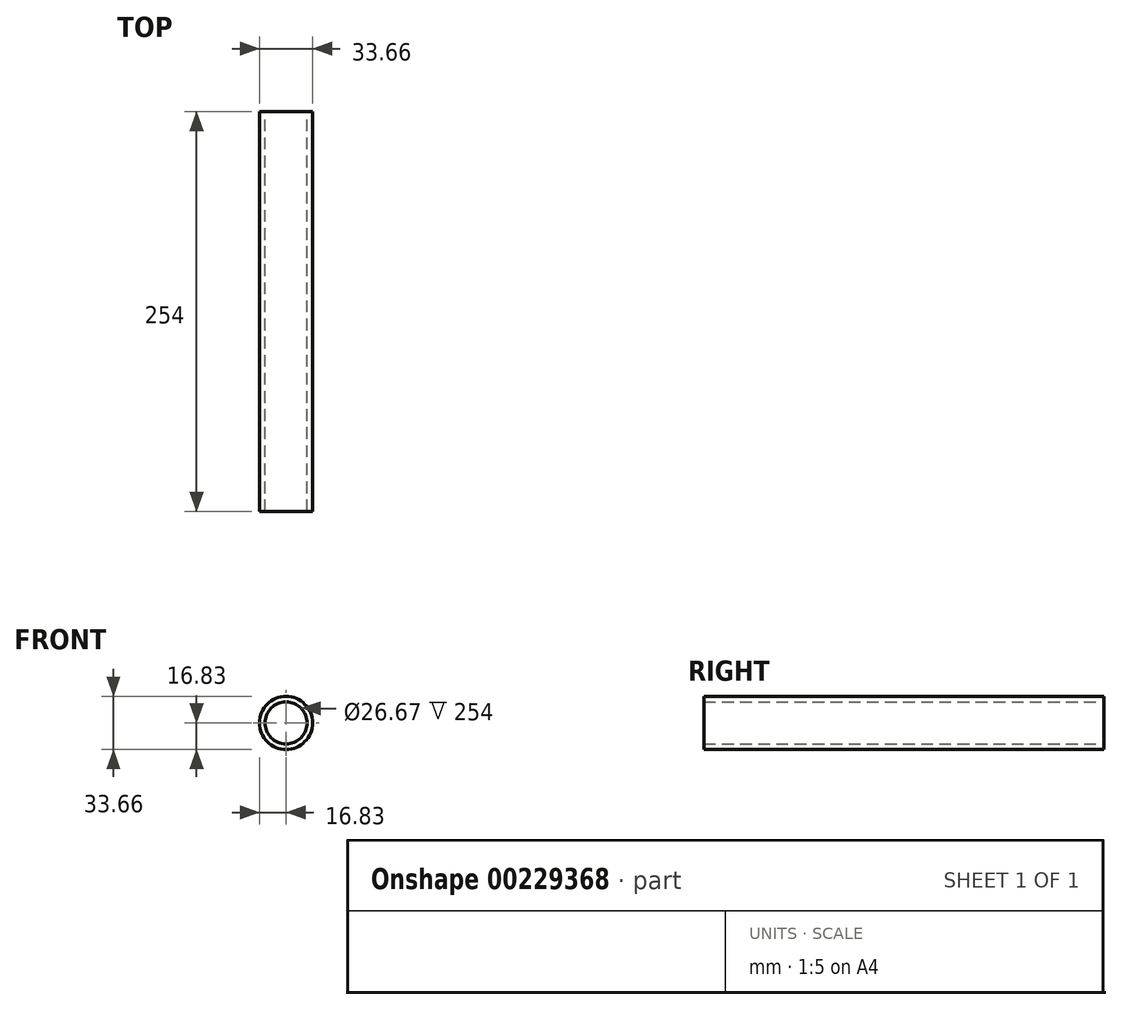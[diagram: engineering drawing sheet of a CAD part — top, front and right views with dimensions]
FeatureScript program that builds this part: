
annotation { "Feature Type Name" : "Feature", "Feature Type Description" : "" }
export const myFeature = defineFeature(function(context is Context, id is Id, definition is map)
    precondition{}
    {
        {
            var Q0;
            Q0=qCreatedBy(makeId("Front.planeOp"),FACE);
            var sketch = newSketch(context, id + "F0", { "sketchPlane" : qUnion([Q0])});
            skCircle(sketch, "E0", {"center": v(0, 0) * mm, "radius": 13.34 * mm});
            skCircle(sketch, "E1", {"center": v(0, 0) * mm, "radius": 16.83 * mm});
            skSolve(sketch);
        }
        {
            var Q0;
            Q0=makeQuery(id+"F0.imprint","IMPRINT",FACE,{"disambiguationData":[TD([[makeQuery(id+"F0.imprint","IMPRINT",EDGE,{"derivedFrom":sQuery(id+"F0.wireOp",EDGE,"E0")}),-1.0]])]});
            extrude(context, id + "F1", {"entities" : qUnion([Q0]), "depth" : 254 * mm});
        }
    });
